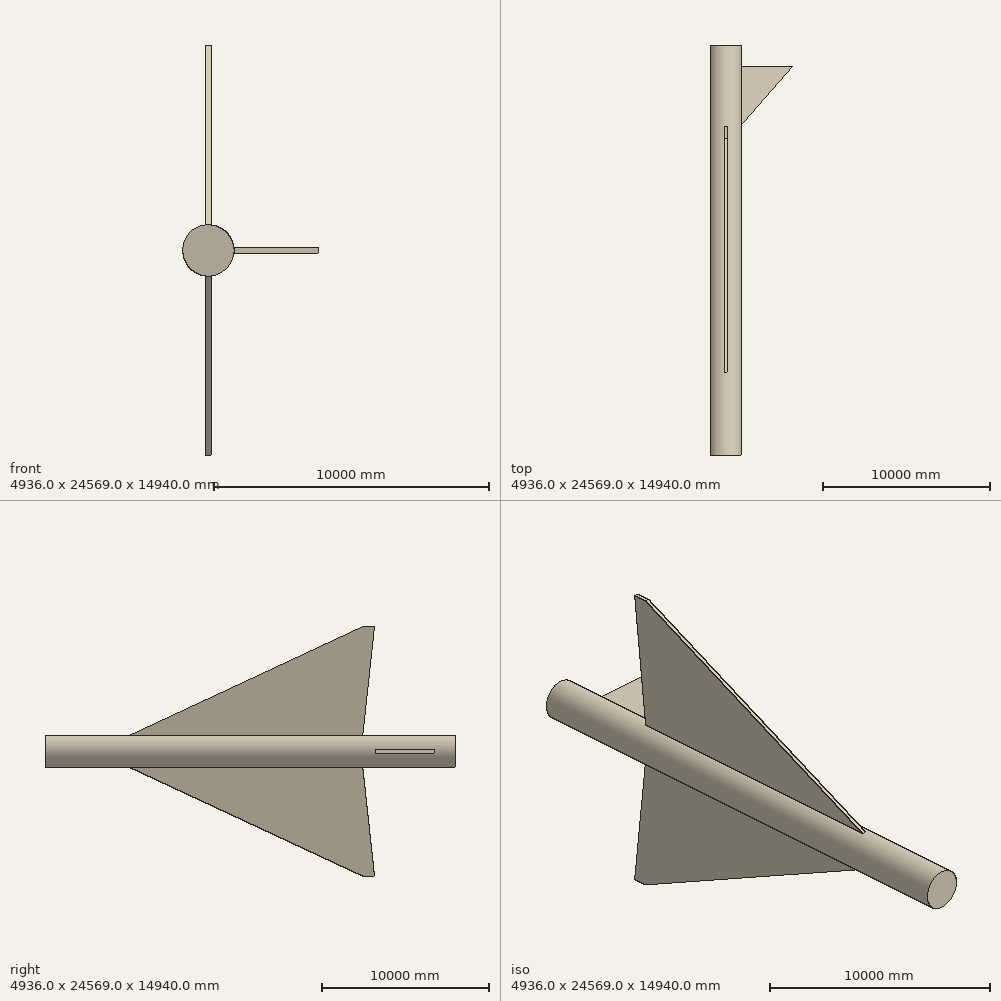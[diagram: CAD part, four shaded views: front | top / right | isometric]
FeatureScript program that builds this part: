
annotation { "Feature Type Name" : "Feature", "Feature Type Description" : "" }
export const myFeature = defineFeature(function(context is Context, id is Id, definition is map)
    precondition{}
    {
        {
            var Q0;
            Q0=qCreatedBy(makeId("Front.planeOp"),FACE);
            var sketch = newSketch(context, id + "F0", { "sketchPlane" : qUnion([Q0])});
            skCircle(sketch, "E0", {"center": v(0, 0) * mm, "radius": 936 * mm});
            skSolve(sketch);
        }
        {
            var Q0;
            Q0=qCreatedBy(makeId("Right.planeOp"),FACE);
            var sketch = newSketch(context, id + "F1", { "sketchPlane" : qUnion([Q0])});
            skPoint(sketch, "E1", {"position": v(0, 0) * mm});
            skPoint(sketch, "E2", {"position": v(0, 936) * mm});
            skPoint(sketch, "E3", {"position": v(0, -936) * mm});
            skPoint(sketch, "E4", {"position": v(14012, 936) * mm});
            skPoint(sketch, "E5", {"position": v(14012, -936) * mm});
            skLineSegment(sketch, "E6", {"start": v(0, 936) * mm, "end": v(14012, 936) * mm});
            skLineSegment(sketch, "E7", {"start": v(14012, -936) * mm, "end": v(0, -936) * mm});
            skLineSegment(sketch, "E8", {"start": v(14012, 936) * mm, "end": v(14012, -936) * mm});
            skLineSegment(sketch, "E9", {"start": v(14012, 936) * mm, "end": v(14012, 7470) * mm});
            skLineSegment(sketch, "E10", {"start": v(14012, -936) * mm, "end": v(14012, -7470) * mm});
            skPoint(sketch, "E10.endSnap0", {"position": v(14012, 0) * mm});
            skLineSegment(sketch, "E11", {"start": v(0, -936) * mm, "end": v(14012, -7470) * mm});
            skLineSegment(sketch, "E12", {"start": v(14012, 7470) * mm, "end": v(0, 936) * mm});
            skSolve(sketch);
        }
        {
            var Q0;
            Q0=qCreatedBy(makeId("Right.planeOp"),FACE);
            var sketch = newSketch(context, id + "F2", { "sketchPlane" : qUnion([Q0])});
            skLineSegment(sketch, "E13", {"start": v(14012, 7470) * mm, "end": v(14718, 7470) * mm});
            skLineSegment(sketch, "E14", {"start": v(14718, 7470) * mm, "end": v(14012, 936) * mm});
            skLineSegment(sketch, "E15", {"start": v(14012, -936) * mm, "end": v(14718, -7470) * mm});
            skLineSegment(sketch, "E16", {"start": v(14012, -7470) * mm, "end": v(14718, -7470) * mm});
            skLineSegment(sketch, "E17", {"start": v(14012, 7470) * mm, "end": v(14012, 936) * mm});
            skLineSegment(sketch, "E18", {"start": v(14012, -936) * mm, "end": v(14012, -7470) * mm});
            skSolve(sketch);
        }
        {
            var Q0;
            Q0=makeQuery(id+"F0.imprint","IMPRINT",FACE,{"disambiguationData":[TD([[makeQuery(id+"F0.imprint","IMPRINT",EDGE,{"derivedFrom":sQuery(id+"F0.wireOp",EDGE,"E0")}),1.0]])]});
            extrude(context, id + "F3", {"entities" : qUnion([Q0]), "oppositeDirection" : true, "depth" : 14012 * mm});
        }
        {
            var Q0;
            Q0 = qSketchRegion(id + "F1", true);
            extrude(context, id + "F4", {"entities" : qUnion([Q0]), "endBound" : BoundingType.SYMMETRIC, "oppositeDirection" : true, "depth" : 200 * mm});
        }
        {
            var Q0;
            Q0 = qSketchRegion(id + "F2", true);
            extrude(context, id + "F5", {"entities" : qUnion([Q0]), "endBound" : BoundingType.SYMMETRIC, "oppositeDirection" : true, "depth" : 200 * mm});
        }
        {
            var Q0;
            Q0=makeQuery(id+"F3.opExtrude","CAP_FACE",FACE,{"disambiguationData":[OSD([sQuery(id+"F0.wireOp",EDGE,"E0")])],"isStart":true});
            extrude(context, id + "F6", {"entities" : qUnion([Q0]), "operationType" : NewBodyOperationType.ADD, "depth" : 5000 * mm});
        }
        {
            var Q0;
            Q0=makeQuery(id+"F3.opExtrude","CAP_FACE",FACE,{"disambiguationData":[OSD([sQuery(id+"F0.wireOp",EDGE,"E0")])],"isStart":false});
            extrude(context, id + "F7", {"entities" : qUnion([Q0]), "operationType" : NewBodyOperationType.ADD, "depth" : 5557 * mm});
        }
        {
            var Q0;
            Q0=qCreatedBy(makeId("Right.planeOp"),FACE);
            var sketch = newSketch(context, id + "F8", { "sketchPlane" : qUnion([Q0])});
            skPoint(sketch, "E19", {"position": v(-5000, 0) * mm});
            skPoint(sketch, "E20", {"position": v(-5000, 936) * mm});
            skPoint(sketch, "E21", {"position": v(-8500, 0) * mm});
            skPoint(sketch, "E22", {"position": v(-5000, -936) * mm});
            skLineSegment(sketch, "E23", {"start": v(-5000, 936) * mm, "end": v(-8500, 0) * mm});
            skLineSegment(sketch, "E24", {"start": v(-5000, 0) * mm, "end": v(-8500, 0) * mm});
            skSolve(sketch);
        }
        {
            var Q0;
            Q0=sQuery(id+"F8.wireOp",EDGE,"E23");
            var Q1;
            Q1=sQuery(id+"F8.wireOp",EDGE,"E24");
            revolve(context, id + "F9", {"bodyType" : ToolBodyType.SURFACE, "surfaceEntities" : qUnion([Q0]), "axis" : qUnion([Q1]), "revolveType" : RevolveType.ONE_DIRECTION, "angle" : 360 * degree});
        }
        {
            var Q0;
            Q0=qCreatedBy(makeId("Top.planeOp"),FACE);
            var sketch = newSketch(context, id + "F10", { "sketchPlane" : qUnion([Q0])});
            skPoint(sketch, "E25", {"position": v(0, 0) * mm});
            skPoint(sketch, "E26", {"position": v(4500, 0) * mm});
            skPoint(sketch, "E27", {"position": v(0, 14791.1) * mm});
            skPoint(sketch, "E28", {"position": v(936, 18291.1) * mm});
            skPoint(sketch, "E29", {"position": v(4000, 18291.1) * mm});
            skLineSegment(sketch, "E30", {"start": v(4000, 18291.1) * mm, "end": v(936, 18291.1) * mm});
            skPoint(sketch, "E31", {"position": v(936, 14791.1) * mm});
            skLineSegment(sketch, "E32", {"start": v(936, 14791.1) * mm, "end": v(4000, 18291.1) * mm});
            skLineSegment(sketch, "E33", {"start": v(936, 14791.1) * mm, "end": v(936, 18291.1) * mm});
            skSolve(sketch);
        }
        {
            var Q0;
            Q0=makeQuery(id+"F10.imprint","IMPRINT",FACE,{"disambiguationData":[TD([[makeQuery(id+"F10.imprint","IMPRINT",EDGE,{"derivedFrom":sQuery(id+"F10.wireOp",EDGE,"E30")}),1.0]])]});
            extrude(context, id + "F11", {"entities" : qUnion([Q0]), "operationType" : NewBodyOperationType.ADD, "endBound" : BoundingType.SYMMETRIC, "depth" : 200 * mm});
        }
    });
